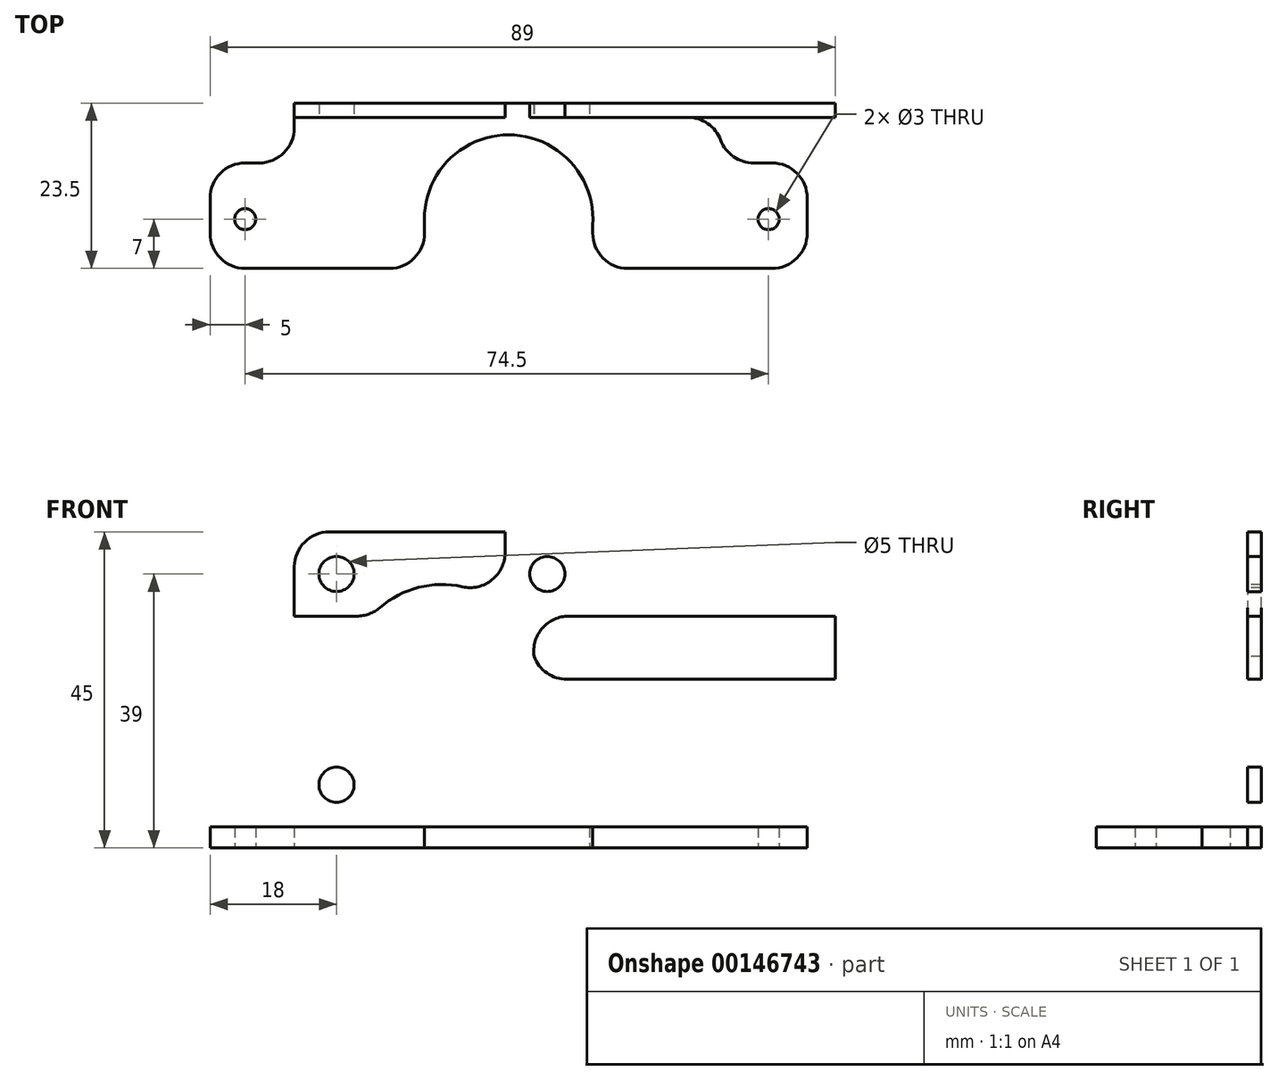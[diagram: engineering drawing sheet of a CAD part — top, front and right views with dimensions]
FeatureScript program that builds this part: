
annotation { "Feature Type Name" : "Feature", "Feature Type Description" : "" }
export const myFeature = defineFeature(function(context is Context, id is Id, definition is map)
    precondition{}
    {
        {
            var Q0;
            Q0=qCreatedBy(makeId("Top.planeOp"),FACE);
            var sketch = newSketch(context, id + "F0", { "sketchPlane" : qUnion([Q0])});
            skLineSegment(sketch, "E0.bottom", {"start": v(-42.5, 15.5) * mm, "end": v(42.5, 15.5) * mm});
            skLineSegment(sketch, "E0.top", {"start": v(-42.5, -15.5) * mm, "end": v(42.5, -15.5) * mm});
            skLineSegment(sketch, "E0.left", {"start": v(-42.5, 15.5) * mm, "end": v(-42.5, -15.5) * mm});
            skLineSegment(sketch, "E0.right", {"start": v(42.5, 15.5) * mm, "end": v(42.5, -15.5) * mm});
            skPoint(sketch, "E0.middle", {"position": v(0, 0) * mm});
            skLineSegment(sketch, "E1", {"start": v(-30.5, 15.5) * mm, "end": v(-30.5, -15.5) * mm});
            skLineSegment(sketch, "E2", {"start": v(30.5, 15.5) * mm, "end": v(30.5, -15.5) * mm});
            skLineSegment(sketch, "E3", {"start": v(-42.5, 7) * mm, "end": v(-30.5, 7) * mm});
            skLineSegment(sketch, "E4", {"start": v(-42.5, -8) * mm, "end": v(-30.5, -8) * mm});
            skLineSegment(sketch, "E5", {"start": v(30.5, 7) * mm, "end": v(42.5, 7) * mm});
            skLineSegment(sketch, "E6", {"start": v(30.5, -8) * mm, "end": v(42.5, -8) * mm});
            skPoint(sketch, "E7", {"position": v(-37.5, -1) * mm});
            skPoint(sketch, "E8", {"position": v(37, -1) * mm});
            skCircle(sketch, "E9", {"center": v(0, -1) * mm, "radius": 12 * mm});
            skLineSegment(sketch, "E10", {"start": v(-30.5, -8) * mm, "end": v(-9.75, -8) * mm});
            skLineSegment(sketch, "E11", {"start": v(30.5, -8) * mm, "end": v(9.75, -8) * mm});
            skLineSegment(sketch, "E12", {"start": v(11.96, 0) * mm, "end": v(11.96, -15.5) * mm});
            skLineSegment(sketch, "E13", {"start": v(-11.96, 0) * mm, "end": v(-11.96, -15.5) * mm});
            skLineSegment(sketch, "E14", {"start": v(-30.5, 13.5) * mm, "end": v(11.5, 13.5) * mm});
            skLineSegment(sketch, "E15", {"start": v(11.5, 13.5) * mm, "end": v(11.5, 15.5) * mm});
            skLineSegment(sketch, "E16", {"start": v(11.5, 13.5) * mm, "end": v(30.5, 13.5) * mm});
            skLineSegment(sketch, "E17", {"start": v(-30.5, 15.5) * mm, "end": v(-30.5, 45.5) * mm});
            skLineSegment(sketch, "E18", {"start": v(-30.5, 45.5) * mm, "end": v(11.5, 45.5) * mm});
            skLineSegment(sketch, "E19", {"start": v(11.5, 45.5) * mm, "end": v(11.5, 15.5) * mm});
            skLineSegment(sketch, "E20", {"start": v(11.5, 45.5) * mm, "end": v(13.5, 45.5) * mm});
            skLineSegment(sketch, "E21", {"start": v(13.5, 45.5) * mm, "end": v(13.5, 15.5) * mm});
            skLineSegment(sketch, "E22", {"start": v(-30.5, 45.5) * mm, "end": v(-32.5, 45.5) * mm});
            skLineSegment(sketch, "E23", {"start": v(-32.5, 45.5) * mm, "end": v(-32.5, 15.5) * mm});
            skLineSegment(sketch, "E24", {"start": v(13.5, 15.5) * mm, "end": v(13.5, 7) * mm});
            skLineSegment(sketch, "E25", {"start": v(13.5, 7) * mm, "end": v(30.5, 7) * mm});
            skSolve(sketch);
        }
        {
            var Q0;
            {var subQ0=sQuery(id+"F0.wireOp",EDGE,"E3");Q0=makeQuery(id+"F0.imprint","IMPRINT",FACE,{"disambiguationData":[TD([[makeQuery(id+"F0.imprint","IMPRINT",EDGE,{"derivedFrom":subQ0}),-1.0]])]});}
            var Q1;
            {var subQ0=sQuery(id+"F0.wireOp",EDGE,"E5");Q1=makeQuery(id+"F0.imprint","IMPRINT",FACE,{"disambiguationData":[TD([[makeQuery(id+"F0.imprint","IMPRINT",EDGE,{"derivedFrom":subQ0}),-1.0]])]});}
            var Q2;
            {var subQ0=sQuery(id+"F0.wireOp",EDGE,"E1");var subQ4=sQuery(id+"F0.wireOp",EDGE,"E0.bottom");var subQ5=makeQuery(id+"F0.imprint","INTERSECT",VERTEX,{"derivedFrom":[subQ4,subQ0]});Q2=makeQuery(id+"F0.imprint","IMPRINT",FACE,{"disambiguationData":[TD([[makeQuery(id+"F0.imprint","IMPRINT",EDGE,{"disambiguationData":[TD([[subQ5,-1.0]])],"derivedFrom":subQ4}),-1.0]])]});}
            var Q3;
            {var subQ14=sQuery(id+"F0.wireOp",EDGE,"E14");Q3=makeQuery(id+"F0.imprint","IMPRINT",FACE,{"disambiguationData":[TD([[makeQuery(id+"F0.imprint","IMPRINT",EDGE,{"derivedFrom":subQ14}),-1.0]])]});}
            var Q4;
            {var subQ0=sQuery(id+"F0.wireOp",EDGE,"E25");Q4=makeQuery(id+"F0.imprint","IMPRINT",FACE,{"disambiguationData":[TD([[makeQuery(id+"F0.imprint","IMPRINT",EDGE,{"derivedFrom":subQ0}),1.0]])]});}
            extrude(context, id + "F1", {"entities" : qUnion([Q0, Q1, Q2, Q3, Q4]), "depth" : 3 * mm});
        }
        {
            var Q0;
            Q0=sQuery(id+"F0.wireOp",VERTEX,"E7");
            var Q1;
            Q1=sQuery(id+"F0.wireOp",VERTEX,"E8");
            var Q2;
            Q2=makeQuery(id+"F1.opExtrude","SWEPT_BODY",BODY,{"disambiguationData":[OSD([sQuery(id+"F0.wireOp",EDGE,"E0.bottom"),sQuery(id+"F0.wireOp",EDGE,"E0.top"),sQuery(id+"F0.wireOp",EDGE,"E0.left"),sQuery(id+"F0.wireOp",EDGE,"E0.right"),sQuery(id+"F0.wireOp",EDGE,"E1"),sQuery(id+"F0.wireOp",EDGE,"E2"),sQuery(id+"F0.wireOp",EDGE,"E3"),sQuery(id+"F0.wireOp",EDGE,"E4"),sQuery(id+"F0.wireOp",EDGE,"E5"),sQuery(id+"F0.wireOp",EDGE,"E6"),sQuery(id+"F0.wireOp",EDGE,"E9"),sQuery(id+"F0.wireOp",EDGE,"QkqRchIF-WoOi-DezC-sPVn-yj0eXFoTficI"),sQuery(id+"F0.wireOp",EDGE,"FLYyLQyL-dbPL-y8Jy-QD5k-8GlpCZOA5ZKs")])]});
            hole(context, id + "F2", {"style" : HoleStyle.SIMPLE, "endStyle" : HoleEndStyle.BLIND, "oppositeDirection" : true, "holeDiameter" : 3 * mm, "holeDepth" : 10 * mm, "locations" : qUnion([Q0, Q1]), "scope" : qUnion([Q2])});
        }
        {
            var Q0;
            {var subQ4=sQuery(id+"F0.wireOp",EDGE,"E14");Q0=makeQuery(id+"F0.imprint","IMPRINT",FACE,{"disambiguationData":[TD([[makeQuery(id+"F0.imprint","IMPRINT",EDGE,{"derivedFrom":subQ4}),1.0]])]});}
            extrude(context, id + "F3", {"entities" : qUnion([Q0]), "operationType" : NewBodyOperationType.ADD, "depth" : (42 + 3) * mm});
        }
        {
            var Q0;
            Q0=makeQuery(id+"F3.opExtrude","SWEPT_FACE",FACE,{"disambiguationData":[OSD([sQuery(id+"F0.wireOp",EDGE,"E14")])]});
            var sketch = newSketch(context, id + "F4", { "sketchPlane" : qUnion([Q0])});
            skLineSegment(sketch, "E26", {"start": v(-9.5, 45) * mm, "end": v(-9.5, 3) * mm, "construction": true});
            skLineSegment(sketch, "E27", {"start": v(-30.5, 24) * mm, "end": v(11.5, 24) * mm, "construction": true});
            skCircle(sketch, "E28", {"center": v(-9.5, 24) * mm, "radius": 13.5 * mm});
            skCircle(sketch, "E29", {"center": v(-24.5, 39) * mm, "radius": 2.5 * mm});
            skCircle(sketch, "E30.MirrorC", {"center": v(5.5, 39) * mm, "radius": 2.5 * mm});
            skCircle(sketch, "E31.MirrorC", {"center": v(-24.5, 9) * mm, "radius": 2.5 * mm});
            skCircle(sketch, "E32.MirrorC", {"center": v(5.5, 9) * mm, "radius": 2.5 * mm});
            skLineSegment(sketch, "E33", {"start": v(-18.5, 45) * mm, "end": v(-18.5, 34.06) * mm});
            skLineSegment(sketch, "E34.MirrorCS", {"start": v(-0.5, 45) * mm, "end": v(-0.5, 34.06) * mm});
            skLineSegment(sketch, "E35", {"start": v(11.5, 45) * mm, "end": v(46.5, 45) * mm});
            skLineSegment(sketch, "E36", {"start": v(-30.5, 15) * mm, "end": v(-19.56, 15) * mm});
            skLineSegment(sketch, "E37.MirrorCS", {"start": v(11.5, 15) * mm, "end": v(0.56, 15) * mm});
            skLineSegment(sketch, "E38.MirrorCS", {"start": v(-30.5, 33) * mm, "end": v(-19.56, 33) * mm});
            skLineSegment(sketch, "E39.MirrorCS", {"start": v(11.5, 33) * mm, "end": v(0.56, 33) * mm});
            skLineSegment(sketch, "E40", {"start": v(11.5, 33) * mm, "end": v(46.5, 33) * mm});
            skLineSegment(sketch, "E41", {"start": v(46.5, 33) * mm, "end": v(46.5, 45) * mm});
            skLineSegment(sketch, "E42", {"start": v(-30.5, 24) * mm, "end": v(-23, 24) * mm});
            skLineSegment(sketch, "E43", {"start": v(11.5, 24) * mm, "end": v(4, 24) * mm});
            skLineSegment(sketch, "E44", {"start": v(11.5, 24) * mm, "end": v(46.5, 24) * mm});
            skLineSegment(sketch, "E45", {"start": v(46.5, 24) * mm, "end": v(46.5, 33) * mm});
            skSolve(sketch);
        }
        {
            var Q0;
            Q0=makeQuery(id+"F4.imprint","IMPRINT",FACE,{"disambiguationData":[TD([[makeQuery(id+"F4.imprint","IMPRINT",EDGE,{"derivedFrom":sQuery(id+"F4.wireOp",EDGE,"E29")}),1.0]])]});
            var Q1;
            Q1=makeQuery(id+"F4.imprint","IMPRINT",FACE,{"disambiguationData":[TD([[makeQuery(id+"F4.imprint","IMPRINT",EDGE,{"derivedFrom":sQuery(id+"F4.wireOp",EDGE,"E30.MirrorC")}),-1.0]])]});
            var Q2;
            Q2=makeQuery(id+"F4.imprint","IMPRINT",FACE,{"disambiguationData":[TD([[makeQuery(id+"F4.imprint","IMPRINT",EDGE,{"derivedFrom":sQuery(id+"F4.wireOp",EDGE,"E31.MirrorC")}),-1.0]])]});
            var Q3;
            Q3=makeQuery(id+"F4.imprint","IMPRINT",FACE,{"disambiguationData":[TD([[makeQuery(id+"F4.imprint","IMPRINT",EDGE,{"derivedFrom":sQuery(id+"F4.wireOp",EDGE,"E32.MirrorC")}),1.0]])]});
            var Q4;
            Q4=makeQuery(id+"F4.imprint","IMPRINT",FACE,{"disambiguationData":[TD([[makeQuery(id+"F4.imprint","IMPRINT",EDGE,{"derivedFrom":sQuery(id+"F4.wireOp",EDGE,"E28")}),1.0]])]});
            var Q5;
            {var subQ0=sQuery(id+"F4.wireOp",EDGE,"E36");Q5=makeQuery(id+"F4.imprint","IMPRINT",FACE,{"disambiguationData":[TD([[makeQuery(id+"F4.imprint","IMPRINT",EDGE,{"derivedFrom":subQ0}),1.0]])]});}
            var Q6;
            {var subQ0=sQuery(id+"F4.wireOp",EDGE,"E37.MirrorCS");Q6=makeQuery(id+"F4.imprint","IMPRINT",FACE,{"disambiguationData":[TD([[makeQuery(id+"F4.imprint","IMPRINT",EDGE,{"derivedFrom":subQ0}),-1.0]])]});}
            var Q7;
            {var subQ0=sQuery(id+"F4.wireOp",EDGE,"E38.MirrorCS");Q7=makeQuery(id+"F4.imprint","IMPRINT",FACE,{"disambiguationData":[TD([[makeQuery(id+"F4.imprint","IMPRINT",EDGE,{"derivedFrom":subQ0}),-1.0]])]});}
            extrude(context, id + "F5", {"entities" : qUnion([Q0, Q1, Q2, Q3, Q4, Q5, Q6, Q7]), "operationType" : NewBodyOperationType.REMOVE, "oppositeDirection" : true, "depth" : 25 * mm});
        }
        {
            var Q0;
            Q0=makeQuery(id+"F1.opExtrude","SWEPT_EDGE",EDGE,{"disambiguationData":[OSD([sQuery(id+"F0.wireOp",EDGE,"E0.left"),sQuery(id+"F0.wireOp",EDGE,"E4")])]});
            var Q1;
            Q1=makeQuery(id+"F1.opExtrude","SWEPT_EDGE",EDGE,{"disambiguationData":[OSD([sQuery(id+"F0.wireOp",EDGE,"E0.left"),sQuery(id+"F0.wireOp",EDGE,"E3")])]});
            var Q2;
            Q2=makeQuery(id+"F1.opExtrude","SWEPT_EDGE",EDGE,{"disambiguationData":[OSD([sQuery(id+"F0.wireOp",EDGE,"E0.top"),sQuery(id+"F0.wireOp",EDGE,"E1")])]});
            var Q3;
            Q3=makeQuery(id+"F1.opExtrude","SWEPT_EDGE",EDGE,{"disambiguationData":[OSD([sQuery(id+"F0.wireOp",EDGE,"E0.top"),sQuery(id+"F0.wireOp",EDGE,"E2")])]});
            var Q4;
            Q4=makeQuery(id+"F1.opExtrude","SWEPT_EDGE",EDGE,{"disambiguationData":[OSD([sQuery(id+"F0.wireOp",EDGE,"E0.right"),sQuery(id+"F0.wireOp",EDGE,"E5")])]});
            var Q5;
            Q5=makeQuery(id+"F1.opExtrude","SWEPT_EDGE",EDGE,{"disambiguationData":[OSD([sQuery(id+"F0.wireOp",EDGE,"E0.right"),sQuery(id+"F0.wireOp",EDGE,"E6")])]});
            var Q6;
            Q6=makeQuery(id+"F1.opExtrude","SWEPT_EDGE",EDGE,{"disambiguationData":[OSD([sQuery(id+"F0.wireOp",EDGE,"E2"),sQuery(id+"F0.wireOp",EDGE,"E16")])]});
            var Q7;
            Q7=makeQuery(id+"F1.opExtrude","SWEPT_EDGE",EDGE,{"disambiguationData":[OSD([sQuery(id+"F0.wireOp",EDGE,"E0.top"),sQuery(id+"F0.wireOp",EDGE,"E13")])]});
            var Q8;
            Q8=makeQuery(id+"F1.opExtrude","SWEPT_EDGE",EDGE,{"disambiguationData":[OSD([sQuery(id+"F0.wireOp",EDGE,"E0.top"),sQuery(id+"F0.wireOp",EDGE,"E12")])]});
            fillet(context, id + "F6", {"entities" : qUnion([Q0, Q1, Q2, Q3, Q4, Q5, Q6, Q7, Q8]), "radius" : 5 * mm, "tangentPropagation" : true, "allowEdgeOverflow" : false});
        }
        {
            var Q0;
            Q0=makeQuery(id+"F1.opExtrude","SWEPT_EDGE",EDGE,{"disambiguationData":[OSD([sQuery(id+"F0.wireOp",EDGE,"E1"),sQuery(id+"F0.wireOp",EDGE,"E3")])]});
            var Q1;
            Q1=makeQuery(id+"F1.opExtrude","SWEPT_EDGE",EDGE,{"disambiguationData":[OSD([sQuery(id+"F0.wireOp",EDGE,"E1"),sQuery(id+"F0.wireOp",EDGE,"E4"),sQuery(id+"F0.wireOp",EDGE,"E10")])]});
            var Q2;
            Q2=makeQuery(id+"F1.opExtrude","SWEPT_EDGE",EDGE,{"disambiguationData":[OSD([sQuery(id+"F0.wireOp",EDGE,"E2"),sQuery(id+"F0.wireOp",EDGE,"E6"),sQuery(id+"F0.wireOp",EDGE,"E11")])]});
            var Q3;
            Q3=makeQuery(id+"F1.opExtrude","SWEPT_EDGE",EDGE,{"disambiguationData":[OSD([sQuery(id+"F0.wireOp",EDGE,"E2"),sQuery(id+"F0.wireOp",EDGE,"E5")])]});
            var Q4;
            Q4=makeQuery(id+"F1.opExtrude","SWEPT_EDGE",EDGE,{"disambiguationData":[OSD([sQuery(id+"F0.wireOp",EDGE,"E24"),sQuery(id+"F0.wireOp",EDGE,"E25")])]});
            fillet(context, id + "F7", {"entities" : qUnion([Q0, Q1, Q2, Q3, Q4]), "radius" : 5 * mm, "tangentPropagation" : true, "allowEdgeOverflow" : false});
        }
        {
            var Q0;
            {var subQ0=sQuery(id+"F4.wireOp",EDGE,"E40");Q0=makeQuery(id+"F4.imprint","IMPRINT",FACE,{"disambiguationData":[TD([[makeQuery(id+"F4.imprint","IMPRINT",EDGE,{"derivedFrom":subQ0}),-1.0]])]});}
            extrude(context, id + "F8", {"entities" : qUnion([Q0]), "operationType" : NewBodyOperationType.ADD, "oppositeDirection" : true, "depth" : 2 * mm});
        }
        {
            var Q0;
            Q0=makeQuery(id+"F5.boolean.opBoolean","COPY",EDGE,{"derivedFrom":makeQuery(id+"F5.opExtrude","SWEPT_EDGE",EDGE,{"disambiguationData":[OSD([sQuery(id+"F0.wireOp",EDGE,"E1"),sQuery(id+"F0.wireOp",EDGE,"E14"),sQuery(id+"F4.wireOp",EDGE,"E38.MirrorCS")])]})});
            var Q1;
            Q1=makeQuery(id+"F3.opExtrude","CAP_EDGE",EDGE,{"disambiguationData":[OSD([sQuery(id+"F0.wireOp",EDGE,"E1")])],"isStart":false});
            var Q2;
            Q2=makeQuery(id+"F5.boolean.opBoolean","COPY",EDGE,{"derivedFrom":makeQuery(id+"F5.opExtrude","SWEPT_EDGE",EDGE,{"disambiguationData":[OSD([sQuery(id+"F4.wireOp",EDGE,"E28"),sQuery(id+"F4.wireOp",EDGE,"E38.MirrorCS")])]})});
            var Q3;
            Q3=makeQuery(id+"F5.boolean.opBoolean","COPY",EDGE,{"derivedFrom":makeQuery(id+"F5.opExtrude","SWEPT_EDGE",EDGE,{"disambiguationData":[OSD([sQuery(id+"F4.wireOp",EDGE,"E28"),sQuery(id+"F4.wireOp",EDGE,"E39.MirrorCS")])]})});
            var Q4;
            Q4=makeQuery(id+"F5.boolean.opBoolean","COPY",EDGE,{"derivedFrom":makeQuery(id+"F5.opExtrude","SWEPT_EDGE",EDGE,{"disambiguationData":[OSD([sQuery(id+"F0.wireOp",EDGE,"E14"),sQuery(id+"F0.wireOp",EDGE,"E15"),sQuery(id+"F0.wireOp",EDGE,"E16"),sQuery(id+"F4.wireOp",EDGE,"E37.MirrorCS")])]})});
            var Q5;
            Q5=makeQuery(id+"F5.boolean.opBoolean","COPY",EDGE,{"derivedFrom":makeQuery(id+"F5.opExtrude","SWEPT_EDGE",EDGE,{"disambiguationData":[OSD([sQuery(id+"F4.wireOp",EDGE,"E28"),sQuery(id+"F4.wireOp",EDGE,"E37.MirrorCS")])]})});
            var Q6;
            Q6=makeQuery(id+"F5.boolean.opBoolean","COPY",EDGE,{"derivedFrom":makeQuery(id+"F5.opExtrude","SWEPT_EDGE",EDGE,{"disambiguationData":[OSD([sQuery(id+"F4.wireOp",EDGE,"E28"),sQuery(id+"F4.wireOp",EDGE,"E36")])]})});
            var Q7;
            Q7=makeQuery(id+"F5.boolean.opBoolean","COPY",EDGE,{"derivedFrom":makeQuery(id+"F5.opExtrude","SWEPT_EDGE",EDGE,{"disambiguationData":[OSD([sQuery(id+"F0.wireOp",EDGE,"E1"),sQuery(id+"F0.wireOp",EDGE,"E14"),sQuery(id+"F4.wireOp",EDGE,"E36")])]})});
            var Q8;
            Q8=makeQuery(id+"F3.opExtrude","CAP_EDGE",EDGE,{"disambiguationData":[OSD([sQuery(id+"F0.wireOp",EDGE,"E15")])],"isStart":false});
            var Q9;
            Q9=makeQuery(id+"F8.opExtrude","SWEPT_EDGE",EDGE,{"disambiguationData":[OSD([sQuery(id+"F0.wireOp",EDGE,"E14"),sQuery(id+"F0.wireOp",EDGE,"E15"),sQuery(id+"F0.wireOp",EDGE,"E16"),sQuery(id+"F4.wireOp",EDGE,"E39.MirrorCS"),sQuery(id+"F4.wireOp",EDGE,"E40")])]});
            fillet(context, id + "F9", {"entities" : qUnion([Q0, Q1, Q2, Q3, Q4, Q5, Q6, Q7, Q8, Q9]), "radius" : 5 * mm, "tangentPropagation" : true, "allowEdgeOverflow" : false});
        }
    });
